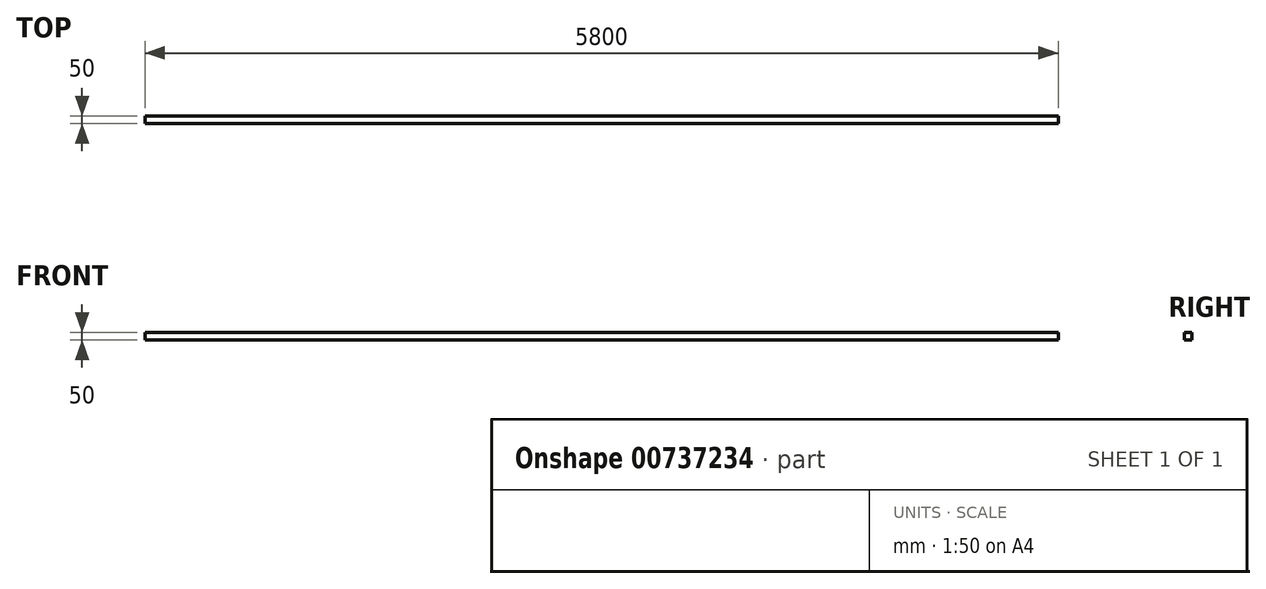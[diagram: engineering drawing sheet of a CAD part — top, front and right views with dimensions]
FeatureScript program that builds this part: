
annotation { "Feature Type Name" : "Feature", "Feature Type Description" : "" }
export const myFeature = defineFeature(function(context is Context, id is Id, definition is map)
    precondition{}
    {
        {
            var Q0;
            Q0=qCreatedBy(makeId("Right.planeOp"),FACE);
            var sketch = newSketch(context, id + "F0", { "sketchPlane" : qUnion([Q0])});
            skLineSegment(sketch, "E0.bottom", {"start": v(0, 0) * mm, "end": v(50, 0) * mm});
            skLineSegment(sketch, "E0.top", {"start": v(0, 50) * mm, "end": v(50, 50) * mm});
            skLineSegment(sketch, "E0.left", {"start": v(0, 0) * mm, "end": v(0, 50) * mm});
            skLineSegment(sketch, "E0.right", {"start": v(50, 0) * mm, "end": v(50, 50) * mm});
            skSolve(sketch);
        }
        {
            var Q0;
            Q0=makeQuery(id+"F0.imprint","IMPRINT",FACE,{"disambiguationData":[TD([[makeQuery(id+"F0.imprint","IMPRINT",EDGE,{"derivedFrom":sQuery(id+"F0.wireOp",EDGE,"E0.bottom")}),1.0]])]});
            extrude(context, id + "F1", {"entities" : qUnion([Q0]), "depth" : 5800 * mm, "offsetDistance" : 25 * mm});
        }
    });
